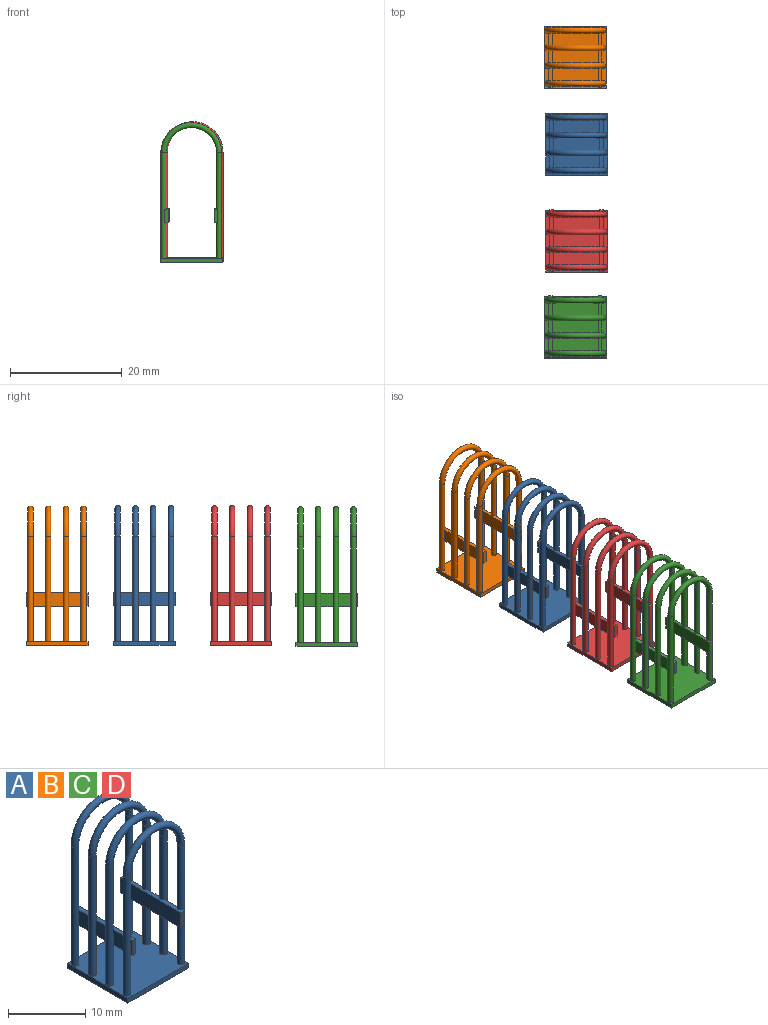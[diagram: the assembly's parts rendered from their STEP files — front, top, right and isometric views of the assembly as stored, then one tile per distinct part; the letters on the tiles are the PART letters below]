
ASSEMBLY  parts=4 mates=1
PART A: 38 faces, bbox 11.8x11.1x25.5 mm
  f0: plane 11.14x11.11mm, normal (0,0,1), area 117.6mm2, adj f1,f2,f4,f5,f6,f7,f11,f12
  f1: cylinder r=0.5mm len=18.85mm, axis (0,0,1), area 55.9mm2, adj f0,f3,f9,f25,f26,f27
  f2: cylinder r=0.5mm len=18.85mm, axis (0,0,-1), area 55.9mm2, adj f0,f3,f10,f15,f32,f34
  f3: torus R=4.96mm, axis (0,-1,0), area 48.6mm2, adj f1,f2
  f4: plane 11.11x0.76mm, normal (-1,0,0), area 8.5mm2, adj f0,f5,f7,f8
  f5: plane 11.14x0.76mm, normal (0,-1,0), area 8.5mm2, adj f0,f4,f6,f8
  f6: plane 11.11x0.76mm, normal (1,0,0), area 8.5mm2, adj f0,f5,f7,f8
  f7: plane 11.14x0.76mm, normal (0,1,0), area 8.5mm2, adj f0,f4,f6,f8
  f8: plane 11.14x11.11mm, normal (0,0,-1), area 123.7mm2, adj f4,f5,f6,f7
  f9: plane 2.38x2.25mm, normal (1,0,0), area 5.4mm2, adj f1,f11,f25,f27
  f10: plane 2.38x0.33mm, normal (-1,0,0), area 0.8mm2, adj f2,f32,f34,f37
  f11: cylinder r=0.5mm len=18.85mm, axis (0,0,1), area 55.9mm2, adj f0,f9,f13,f14,f25,f27
  f12: cylinder r=0.5mm len=18.85mm, axis (0,0,-1), area 55.9mm2, adj f0,f13,f15,f20,f32,f34
  f13: torus R=4.96mm, axis (0,-1,0), area 48.6mm2, adj f11,f12
  f14: plane 2.38x2.25mm, normal (1,0,0), area 5.4mm2, adj f11,f16,f25,f27
  f15: plane 2.38x2.25mm, normal (-1,0,0), area 5.4mm2, adj f2,f12,f32,f34
  f16: cylinder r=0.5mm len=18.85mm, axis (0,0,1), area 55.9mm2, adj f0,f14,f18,f19,f25,f27
  f17: cylinder r=0.5mm len=18.85mm, axis (0,0,-1), area 55.9mm2, adj f0,f18,f20,f31,f32,f34
  f18: torus R=4.96mm, axis (0,-1,0), area 48.6mm2, adj f16,f17
  f19: plane 2.38x2.25mm, normal (1,0,0), area 5.4mm2, adj f16,f22,f25,f27
  f20: plane 2.38x2.25mm, normal (-1,0,0), area 5.4mm2, adj f12,f17,f32,f34
  f21: cylinder r=0.5mm len=18.85mm, axis (0,0,-1), area 55.9mm2, adj f0,f23,f31,f32,f33,f34
  f22: cylinder r=0.5mm len=18.85mm, axis (0,0,1), area 55.9mm2, adj f0,f19,f23,f24,f25,f27
  f23: torus R=4.96mm, axis (0,-1,0), area 48.6mm2, adj f21,f22
  f24: plane 2.38x0.33mm, normal (1,0,0), area 0.8mm2, adj f22,f25,f27,f29
  f25: plane 11.11x0.64mm, normal (0,0,1), area 6.2mm2, adj f1,f9,f11,f14,f16,f19,f22,f24
  f26: plane 2.38x0.33mm, normal (1,0,0), area 0.8mm2, adj f1,f25,f27,f30
  f27: plane 11.11x0.64mm, normal (0,0,-1), area 6.2mm2, adj f1,f9,f11,f14,f16,f19,f22,f24
  f28: plane 11.11x2.38mm, normal (-1,0,0), area 26.5mm2, adj f25,f27,f29,f30
  f29: plane 2.38x0.64mm, normal (0,-1,0), area 1.5mm2, adj f24,f25,f27,f28
  f30: plane 2.38x0.64mm, normal (0,1,0), area 1.5mm2, adj f25,f26,f27,f28
  f31: plane 2.38x2.25mm, normal (-1,0,0), area 5.4mm2, adj f17,f21,f32,f34
  f32: plane 11.11x0.64mm, normal (0,0,-1), area 6.2mm2, adj f2,f10,f12,f15,f17,f20,f21,f31
  f33: plane 2.38x0.33mm, normal (-1,0,0), area 0.8mm2, adj f21,f32,f34,f36
  f34: plane 11.11x0.64mm, normal (0,0,1), area 6.2mm2, adj f2,f10,f12,f15,f17,f20,f21,f31
  f35: plane 11.11x2.38mm, normal (1,0,0), area 26.5mm2, adj f32,f34,f36,f37
  f36: plane 2.38x0.64mm, normal (0,-1,0), area 1.5mm2, adj f32,f33,f34,f35
  f37: plane 2.38x0.64mm, normal (0,1,0), area 1.5mm2, adj f10,f32,f34,f35
PART B: same geometry as A
PART C: same geometry as A
PART D: same geometry as A
PLACE A t=(0.22,22.06,-11.77)mm
PLACE B t=(-0.01,37.71,-11.85)mm
PLACE C t=(-0.01,-10.71,-11.94)mm
PLACE D t=(0.22,4.71,-11.77)mm
MATE planar D.f6 <-> A.f6  axis (1,0,0) through (5.8,-0.05,-12.15)mm
